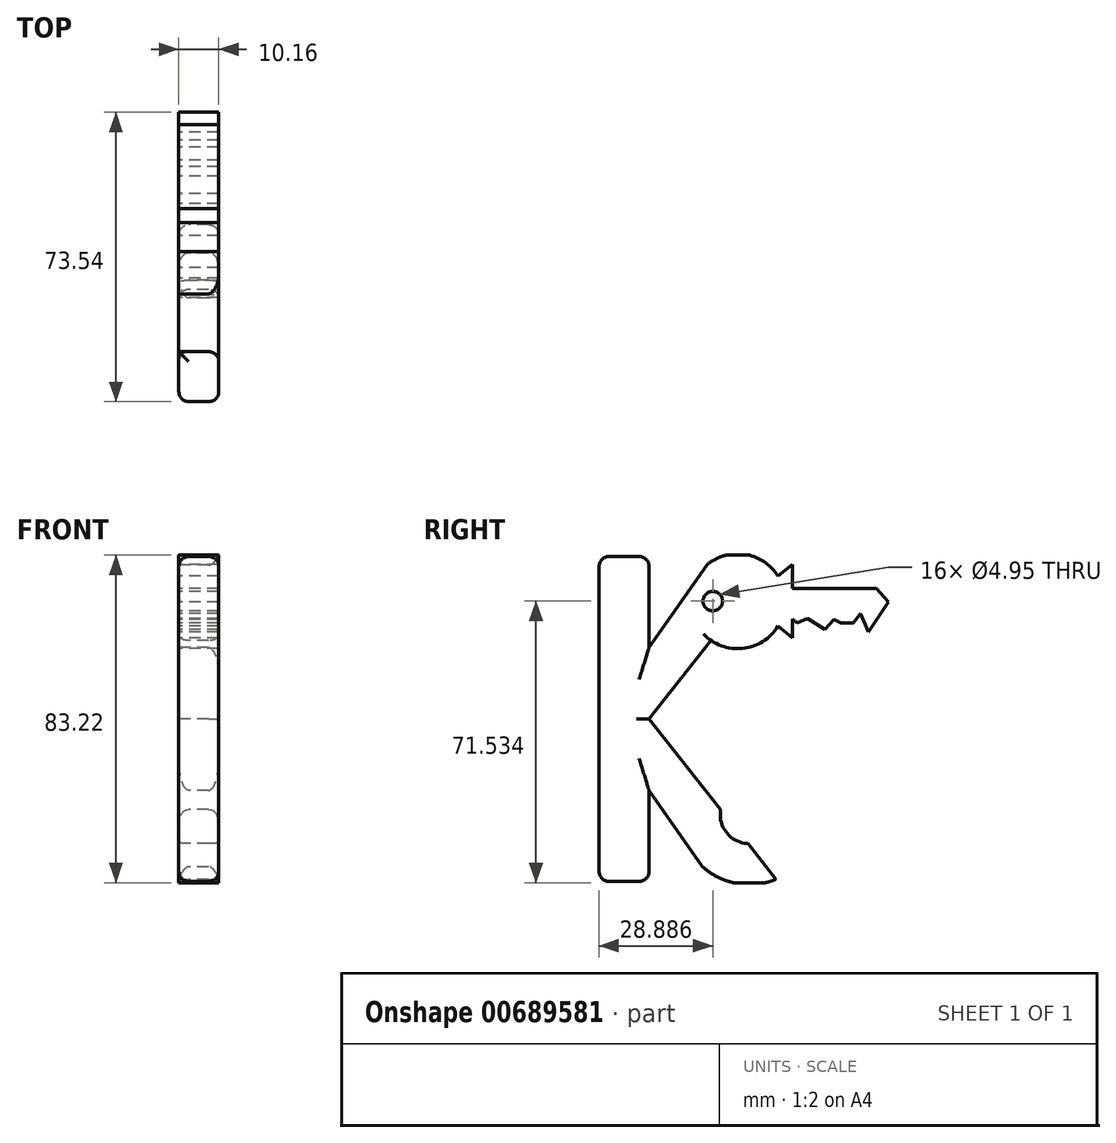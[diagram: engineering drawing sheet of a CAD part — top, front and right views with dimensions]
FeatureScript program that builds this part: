
annotation { "Feature Type Name" : "Feature", "Feature Type Description" : "" }
export const myFeature = defineFeature(function(context is Context, id is Id, definition is map)
    precondition{}
    {
        {
            var Q0;
            Q0=qCreatedBy(makeId("Right.planeOp"),FACE);
            var sketch = newSketch(context, id + "F0", { "sketchPlane" : qUnion([Q0])});
            skLineSegment(sketch, "E0.bottom", {"start": v(-25.49, 41.28) * mm, "end": v(-12.79, 41.28) * mm});
            skLineSegment(sketch, "E0.top", {"start": v(-25.49, -41.28) * mm, "end": v(-12.79, -41.28) * mm});
            skLineSegment(sketch, "E0.left", {"start": v(-25.49, 41.28) * mm, "end": v(-25.49, -41.28) * mm});
            skLineSegment(sketch, "E0.right", {"start": v(-12.79, 41.28) * mm, "end": v(-12.79, -41.28) * mm});
            skPoint(sketch, "E0.middle", {"position": v(-19.14, 0) * mm});
            skLineSegment(sketch, "E1", {"start": v(-25.49, 0) * mm, "end": v(3.65, 41.61) * mm});
            skLineSegment(sketch, "E2", {"start": v(3.65, 41.61) * mm, "end": v(20.16, 41.61) * mm});
            skLineSegment(sketch, "E3", {"start": v(20.16, 41.61) * mm, "end": v(-12.79, 0) * mm});
            skLineSegment(sketch, "E4", {"start": v(-25.49, 0) * mm, "end": v(3.65, -41.61) * mm});
            skLineSegment(sketch, "E5", {"start": v(3.65, -41.61) * mm, "end": v(20.16, -41.61) * mm});
            skLineSegment(sketch, "E6", {"start": v(20.16, -41.61) * mm, "end": v(-12.79, 0) * mm});
            skCircle(sketch, "E7", {"center": v(12.67, -24.3) * mm, "radius": 17.78 * mm});
            skPoint(sketch, "E7.first.point", {"position": v(-3.83, -30.93) * mm});
            skPoint(sketch, "E7.second.point", {"position": v(29.71, -19.23) * mm});
            skPoint(sketch, "E7.third.point", {"position": v(4.01, -8.77) * mm});
            skCircle(sketch, "E8", {"center": v(12.67, -24.3) * mm, "radius": 7.38 * mm});
            skCircle(sketch, "E9", {"center": v(9.73, 29.92) * mm, "radius": 12.07 * mm});
            skPoint(sketch, "E9.first.point", {"position": v(-1.58, 34.14) * mm});
            skPoint(sketch, "E9.second.point", {"position": v(21.07, 25.81) * mm});
            skPoint(sketch, "E9.third.point", {"position": v(12.71, 41.61) * mm});
            skCircle(sketch, "E10", {"center": v(3.4, 29.92) * mm, "radius": 2.48 * mm});
            skLineSegment(sketch, "E11.bottom", {"start": v(19.98, 36.28) * mm, "end": v(23.6, 36.28) * mm});
            skLineSegment(sketch, "E11.top", {"start": v(19.98, 23.57) * mm, "end": v(23.6, 23.57) * mm});
            skLineSegment(sketch, "E11.left", {"start": v(19.98, 36.28) * mm, "end": v(19.98, 23.57) * mm});
            skLineSegment(sketch, "E11.right", {"start": v(23.6, 36.28) * mm, "end": v(23.6, 23.57) * mm});
            skPoint(sketch, "E11.middle", {"position": v(21.8, 29.92) * mm});
            skLineSegment(sketch, "E12", {"start": v(19.98, 36.28) * mm, "end": v(23.6, 39.31) * mm});
            skLineSegment(sketch, "E13", {"start": v(23.6, 39.31) * mm, "end": v(23.6, 36.28) * mm});
            skLineSegment(sketch, "E14", {"start": v(19.98, 23.57) * mm, "end": v(23.6, 20.54) * mm});
            skLineSegment(sketch, "E15", {"start": v(23.6, 20.54) * mm, "end": v(23.6, 23.57) * mm});
            skLineSegment(sketch, "E16.bottom", {"start": v(22.11, 33.1) * mm, "end": v(44.97, 33.1) * mm});
            skLineSegment(sketch, "E16.top", {"start": v(22.11, 26.75) * mm, "end": v(44.97, 26.75) * mm});
            skLineSegment(sketch, "E16.left", {"start": v(22.11, 33.1) * mm, "end": v(22.11, 26.75) * mm});
            skLineSegment(sketch, "E16.right", {"start": v(44.97, 33.1) * mm, "end": v(44.97, 26.75) * mm});
            skPoint(sketch, "E16.middle", {"position": v(33.54, 29.92) * mm});
            skLineSegment(sketch, "E17", {"start": v(44.97, 33.1) * mm, "end": v(48.05, 29.74) * mm});
            skLineSegment(sketch, "E18", {"start": v(48.05, 29.74) * mm, "end": v(43, 22.11) * mm});
            skLineSegment(sketch, "E19", {"start": v(43, 22.11) * mm, "end": v(40.93, 26.75) * mm});
            skLineSegment(sketch, "E20", {"start": v(40.93, 26.75) * mm, "end": v(39.2, 24.38) * mm});
            skLineSegment(sketch, "E21", {"start": v(39.2, 24.38) * mm, "end": v(35.95, 24.38) * mm});
            skLineSegment(sketch, "E22", {"start": v(35.95, 24.38) * mm, "end": v(34.21, 25.32) * mm});
            skLineSegment(sketch, "E23", {"start": v(34.21, 25.32) * mm, "end": v(31.84, 22.8) * mm});
            skLineSegment(sketch, "E24", {"start": v(31.84, 22.8) * mm, "end": v(27.43, 25.48) * mm});
            skLineSegment(sketch, "E25", {"start": v(27.43, 25.48) * mm, "end": v(24.8, 24.38) * mm});
            skLineSegment(sketch, "E26", {"start": v(24.8, 24.38) * mm, "end": v(22.11, 26.75) * mm});
            skPoint(sketch, "E27.endSnap0", {"position": v(41.97, 24.43) * mm});
            skSolve(sketch);
        }
        {
            var Q0;
            {var subQ0=sQuery(id+"F0.wireOp",EDGE,"E0.bottom");Q0=makeQuery(id+"F0.imprint","IMPRINT",FACE,{"disambiguationData":[TD([[makeQuery(id+"F0.imprint","IMPRINT",EDGE,{"derivedFrom":subQ0}),-1.0]])]});}
            var Q1;
            {var subQ0=sQuery(id+"F0.wireOp",EDGE,"E0.right");var subQ2=sQuery(id+"F0.wireOp",EDGE,"E1");var subQ3=makeQuery(id+"F0.imprint","INTERSECT",VERTEX,{"derivedFrom":[subQ0,subQ2]});Q1=makeQuery(id+"F0.imprint","IMPRINT",FACE,{"disambiguationData":[TD([[makeQuery(id+"F0.imprint","IMPRINT",EDGE,{"disambiguationData":[TD([[subQ3,-1.0]])],"derivedFrom":subQ0}),-1.0]])]});}
            var Q2;
            {var subQ1=sQuery(id+"F0.wireOp",EDGE,"E0.right");var subQ3=sQuery(id+"F0.wireOp",EDGE,"E4");var subQ4=makeQuery(id+"F0.imprint","INTERSECT",VERTEX,{"derivedFrom":[subQ1,subQ3]});Q2=makeQuery(id+"F0.imprint","IMPRINT",FACE,{"disambiguationData":[TD([[makeQuery(id+"F0.imprint","IMPRINT",EDGE,{"disambiguationData":[TD([[subQ4,-1.0]])],"derivedFrom":subQ3}),1.0]])]});}
            var Q3;
            {var subQ0=sQuery(id+"F0.wireOp",EDGE,"E0.top");Q3=makeQuery(id+"F0.imprint","IMPRINT",FACE,{"disambiguationData":[TD([[makeQuery(id+"F0.imprint","IMPRINT",EDGE,{"derivedFrom":subQ0}),1.0]])]});}
            var Q4;
            {var subQ0=sQuery(id+"F0.wireOp",EDGE,"E7");var subQ10=sQuery(id+"F0.wireOp",EDGE,"E4");var subQ11=makeQuery(id+"F0.imprint","INTERSECT",VERTEX,{"disambiguationData":[OD(0.0)],"derivedFrom":[subQ10,subQ0]});Q4=makeQuery(id+"F0.imprint","IMPRINT",FACE,{"disambiguationData":[TD([[makeQuery(id+"F0.imprint","IMPRINT",EDGE,{"disambiguationData":[TD([[subQ11,-1.0]])],"derivedFrom":subQ10}),1.0]])]});}
            var Q5;
            {var subQ0=sQuery(id+"F0.wireOp",EDGE,"E7");var subQ1=sQuery(id+"F0.wireOp",EDGE,"E6");var subQ2=makeQuery(id+"F0.imprint","INTERSECT",VERTEX,{"disambiguationData":[OD(0.0)],"derivedFrom":[subQ1,subQ0]});Q5=makeQuery(id+"F0.imprint","IMPRINT",FACE,{"disambiguationData":[TD([[makeQuery(id+"F0.imprint","IMPRINT",EDGE,{"disambiguationData":[TD([[subQ2,-1.0]])],"derivedFrom":subQ1}),-1.0]])]});}
            var Q6;
            {var subQ1=sQuery(id+"F0.wireOp",EDGE,"E0.right");var subQ3=sQuery(id+"F0.wireOp",EDGE,"E1");var subQ4=makeQuery(id+"F0.imprint","INTERSECT",VERTEX,{"derivedFrom":[subQ1,subQ3]});Q6=makeQuery(id+"F0.imprint","IMPRINT",FACE,{"disambiguationData":[TD([[makeQuery(id+"F0.imprint","IMPRINT",EDGE,{"disambiguationData":[TD([[subQ4,-1.0]])],"derivedFrom":subQ3}),-1.0]])]});}
            var Q7;
            {var subQ4=sQuery(id+"F0.wireOp",EDGE,"E11.left");Q7=makeQuery(id+"F0.imprint","IMPRINT",FACE,{"disambiguationData":[TD([[makeQuery(id+"F0.imprint","IMPRINT",EDGE,{"derivedFrom":subQ4}),-1.0]])]});}
            var Q8;
            Q8=makeQuery(id+"F0.imprint","IMPRINT",FACE,{"disambiguationData":[TD([[makeQuery(id+"F0.imprint","IMPRINT",EDGE,{"derivedFrom":sQuery(id+"F0.wireOp",EDGE,"E10")}),-1.0]])]});
            var Q9;
            Q9=makeQuery(id+"F0.imprint","IMPRINT",FACE,{"disambiguationData":[TD([[makeQuery(id+"F0.imprint","IMPRINT",EDGE,{"derivedFrom":sQuery(id+"F0.wireOp",EDGE,"E11.bottom")}),1.0]])]});
            var Q10;
            {var subQ1=sQuery(id+"F0.wireOp",EDGE,"E11.bottom");Q10=makeQuery(id+"F0.imprint","IMPRINT",FACE,{"disambiguationData":[TD([[makeQuery(id+"F0.imprint","IMPRINT",EDGE,{"derivedFrom":subQ1}),-1.0]])]});}
            var Q11;
            {var subQ0=sQuery(id+"F0.wireOp",EDGE,"E11.left");Q11=makeQuery(id+"F0.imprint","IMPRINT",FACE,{"disambiguationData":[TD([[makeQuery(id+"F0.imprint","IMPRINT",EDGE,{"derivedFrom":subQ0}),1.0]])]});}
            var Q12;
            {var subQ5=sQuery(id+"F0.wireOp",EDGE,"E16.left");Q12=makeQuery(id+"F0.imprint","IMPRINT",FACE,{"disambiguationData":[TD([[makeQuery(id+"F0.imprint","IMPRINT",EDGE,{"derivedFrom":subQ5}),1.0]])]});}
            var Q13;
            {var subQ0=sQuery(id+"F0.wireOp",EDGE,"E26");var subQ1=sQuery(id+"F0.wireOp",EDGE,"E11.right");var subQ2=makeQuery(id+"F0.imprint","INTERSECT",VERTEX,{"derivedFrom":[subQ1,subQ0]});Q13=makeQuery(id+"F0.imprint","IMPRINT",FACE,{"disambiguationData":[TD([[makeQuery(id+"F0.imprint","IMPRINT",EDGE,{"disambiguationData":[TD([[subQ2,1.0]])],"derivedFrom":subQ1}),-1.0]])]});}
            var Q14;
            Q14=makeQuery(id+"F0.imprint","IMPRINT",FACE,{"disambiguationData":[TD([[makeQuery(id+"F0.imprint","IMPRINT",EDGE,{"derivedFrom":sQuery(id+"F0.wireOp",EDGE,"E11.top")}),-1.0]])]});
            var Q15;
            {var subQ0=sQuery(id+"F0.wireOp",EDGE,"E16.right");Q15=makeQuery(id+"F0.imprint","IMPRINT",FACE,{"disambiguationData":[TD([[makeQuery(id+"F0.imprint","IMPRINT",EDGE,{"derivedFrom":subQ0}),-1.0]])]});}
            var Q16;
            {var subQ0=sQuery(id+"F0.wireOp",EDGE,"E20");Q16=makeQuery(id+"F0.imprint","IMPRINT",FACE,{"disambiguationData":[TD([[makeQuery(id+"F0.imprint","IMPRINT",EDGE,{"derivedFrom":subQ0}),-1.0]])]});}
            var Q17;
            {var subQ0=sQuery(id+"F0.wireOp",EDGE,"E16.right");Q17=makeQuery(id+"F0.imprint","IMPRINT",FACE,{"disambiguationData":[TD([[makeQuery(id+"F0.imprint","IMPRINT",EDGE,{"derivedFrom":subQ0}),1.0]])]});}
            extrude(context, id + "F1", {"entities" : qUnion([Q0, Q1, Q2, Q3, Q4, Q5, Q6, Q7, Q8, Q9, Q10, Q11, Q12, Q13, Q14, Q15, Q16, Q17]), "depth" : 10.16 * mm, "offsetDistance" : 25.4 * mm});
        }
        {
            var Q0;
            Q0=makeQuery(id+"F1.opExtrude","CAP_EDGE",EDGE,{"disambiguationData":[OSD([sQuery(id+"F0.wireOp",EDGE,"E0.left")])],"isStart":false});
            var Q1;
            Q1=makeQuery(id+"F1.opExtrude","CAP_EDGE",EDGE,{"disambiguationData":[OSD([sQuery(id+"F0.wireOp",EDGE,"E0.bottom")])],"isStart":false});
            var Q2;
            Q2=makeQuery(id+"F1.opExtrude","SWEPT_EDGE",EDGE,{"disambiguationData":[OSD([sQuery(id+"F0.wireOp",EDGE,"E0.bottom"),sQuery(id+"F0.wireOp",EDGE,"E0.right")])]});
            var Q3;
            Q3=makeQuery(id+"F1.opExtrude","CAP_EDGE",EDGE,{"disambiguationData":[OSD([sQuery(id+"F0.wireOp",EDGE,"E0.bottom")])],"isStart":true});
            var Q4;
            Q4=makeQuery(id+"F1.opExtrude","SWEPT_EDGE",EDGE,{"disambiguationData":[OSD([sQuery(id+"F0.wireOp",EDGE,"E0.bottom"),sQuery(id+"F0.wireOp",EDGE,"E0.left")])]});
            var Q5;
            Q5=makeQuery(id+"F1.opExtrude","CAP_EDGE",EDGE,{"disambiguationData":[OSD([sQuery(id+"F0.wireOp",EDGE,"E0.left")])],"isStart":true});
            var Q6;
            Q6=makeQuery(id+"F1.opExtrude","CAP_EDGE",EDGE,{"disambiguationData":[OSD([sQuery(id+"F0.wireOp",EDGE,"E1")])],"isStart":false});
            var Q7;
            {var subQ0=sQuery(id+"F0.wireOp",EDGE,"E0.right");Q7=makeQuery(id+"F1.opExtrude","CAP_EDGE",EDGE,{"disambiguationData":[OSD([subQ0]),TDD([makeQuery(id+"F0.imprint","IMPRINT",EDGE,{"disambiguationData":[TD([[makeQuery(id+"F0.imprint","INTERSECT",VERTEX,{"derivedFrom":[sQuery(id+"F0.wireOp",EDGE,"E0.bottom"),subQ0]}),-1.0]])],"derivedFrom":subQ0})])],"isStart":false});}
            var Q8;
            Q8=makeQuery(id+"F1.opExtrude","CAP_EDGE",EDGE,{"disambiguationData":[OSD([sQuery(id+"F0.wireOp",EDGE,"E3")])],"isStart":false});
            var Q9;
            Q9=makeQuery(id+"F1.opExtrude","CAP_EDGE",EDGE,{"disambiguationData":[OSD([sQuery(id+"F0.wireOp",EDGE,"E3")])],"isStart":true});
            var Q10;
            Q10=makeQuery(id+"F1.opExtrude","CAP_EDGE",EDGE,{"disambiguationData":[OSD([sQuery(id+"F0.wireOp",EDGE,"E6")])],"isStart":false});
            var Q11;
            Q11=makeQuery(id+"F1.opExtrude","CAP_EDGE",EDGE,{"disambiguationData":[OSD([sQuery(id+"F0.wireOp",EDGE,"E6")])],"isStart":true});
            var Q12;
            {var subQ0=sQuery(id+"F0.wireOp",EDGE,"E0.right");Q12=makeQuery(id+"F1.opExtrude","CAP_EDGE",EDGE,{"disambiguationData":[OSD([subQ0]),TDD([makeQuery(id+"F0.imprint","IMPRINT",EDGE,{"disambiguationData":[TD([[makeQuery(id+"F0.imprint","INTERSECT",VERTEX,{"derivedFrom":[sQuery(id+"F0.wireOp",EDGE,"E0.top"),subQ0]}),1.0]])],"derivedFrom":subQ0})])],"isStart":false});}
            var Q13;
            {var subQ0=sQuery(id+"F0.wireOp",EDGE,"E0.right");Q13=makeQuery(id+"F1.opExtrude","CAP_EDGE",EDGE,{"disambiguationData":[OSD([subQ0]),TDD([makeQuery(id+"F0.imprint","IMPRINT",EDGE,{"disambiguationData":[TD([[makeQuery(id+"F0.imprint","INTERSECT",VERTEX,{"derivedFrom":[sQuery(id+"F0.wireOp",EDGE,"E0.top"),subQ0]}),1.0]])],"derivedFrom":subQ0})])],"isStart":true});}
            var Q14;
            Q14=makeQuery(id+"F1.opExtrude","CAP_EDGE",EDGE,{"disambiguationData":[OSD([sQuery(id+"F0.wireOp",EDGE,"E0.top")])],"isStart":true});
            var Q15;
            Q15=makeQuery(id+"F1.opExtrude","SWEPT_EDGE",EDGE,{"disambiguationData":[OSD([sQuery(id+"F0.wireOp",EDGE,"E0.top"),sQuery(id+"F0.wireOp",EDGE,"E0.right")])]});
            var Q16;
            Q16=makeQuery(id+"F1.opExtrude","CAP_EDGE",EDGE,{"disambiguationData":[OSD([sQuery(id+"F0.wireOp",EDGE,"E0.top")])],"isStart":false});
            var Q17;
            Q17=makeQuery(id+"F1.opExtrude","SWEPT_EDGE",EDGE,{"disambiguationData":[OSD([sQuery(id+"F0.wireOp",EDGE,"E0.top"),sQuery(id+"F0.wireOp",EDGE,"E0.left")])]});
            var Q18;
            {var subQ0=sQuery(id+"F0.wireOp",EDGE,"E9");var subQ1=sQuery(id+"F0.wireOp",EDGE,"E2");Q18=makeQuery(id+"F1.opExtrude","SWEPT_EDGE",EDGE,{"disambiguationData":[OSD([subQ1,subQ0]),TDD([makeQuery(id+"F0.imprint","INTERSECT",VERTEX,{"disambiguationData":[OD(1.0)],"derivedFrom":[subQ1,subQ0]})])]});}
            var Q19;
            Q19=makeQuery(id+"F1.opExtrude","CAP_EDGE",EDGE,{"disambiguationData":[OSD([sQuery(id+"F0.wireOp",EDGE,"E4")])],"isStart":false});
            var Q20;
            Q20=makeQuery(id+"F1.opExtrude","CAP_EDGE",EDGE,{"disambiguationData":[OSD([sQuery(id+"F0.wireOp",EDGE,"E4")])],"isStart":true});
            fillet(context, id + "F2", {"entities" : qUnion([Q0, Q1, Q2, Q3, Q4, Q5, Q6, Q7, Q8, Q9, Q10, Q11, Q12, Q13, Q14, Q15, Q16, Q17, Q18, Q19, Q20]), "radius" : 2.54 * mm, "tangentPropagation" : true, "allowEdgeOverflow" : false});
        }
    });
